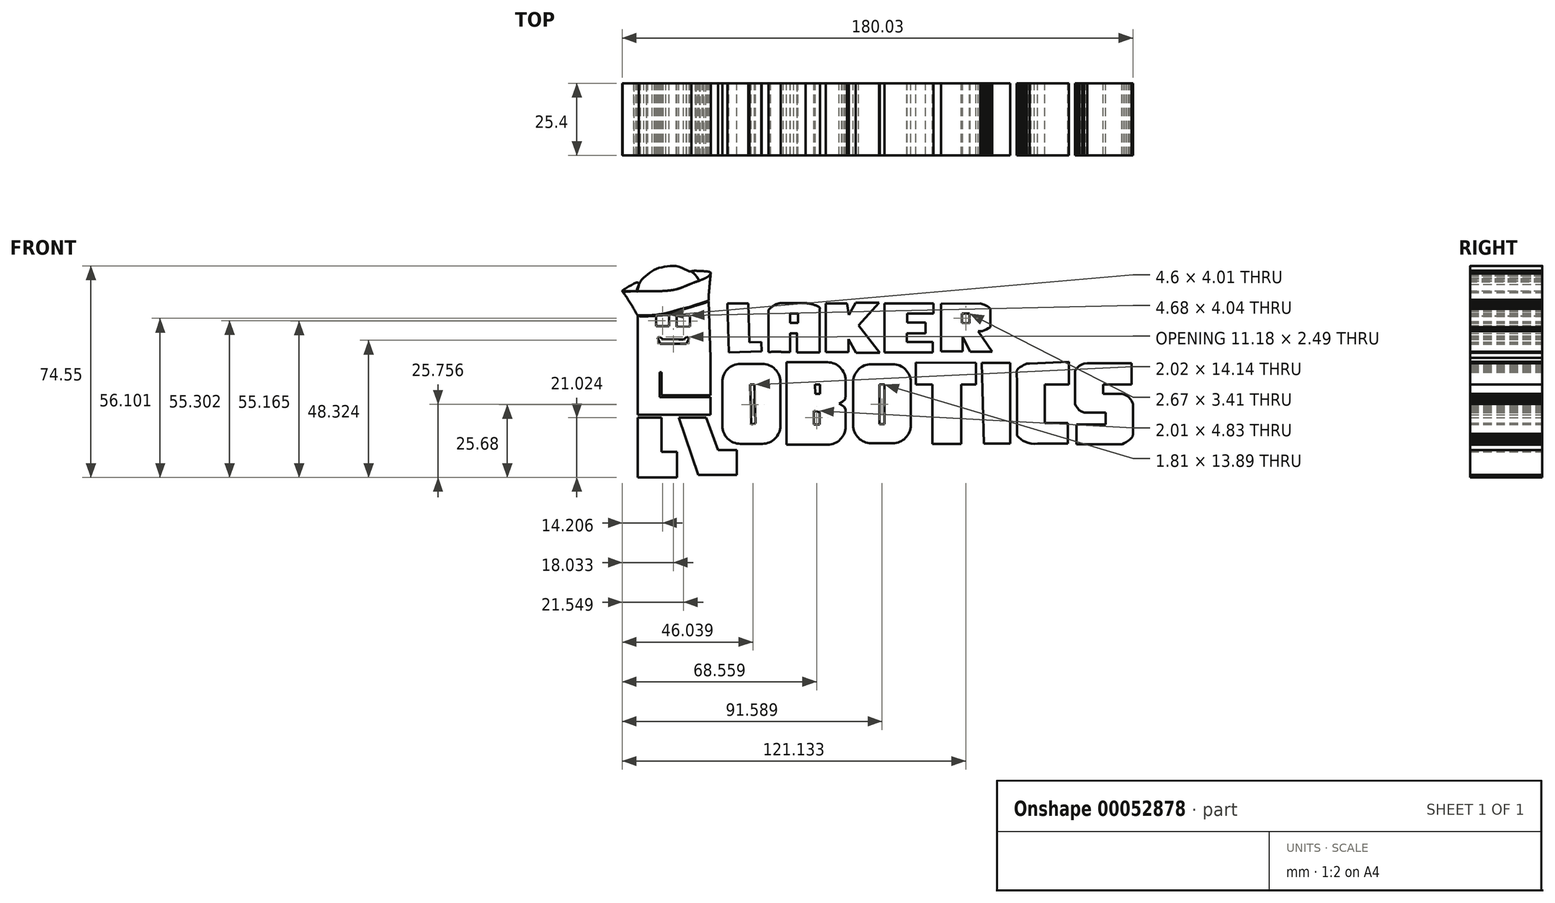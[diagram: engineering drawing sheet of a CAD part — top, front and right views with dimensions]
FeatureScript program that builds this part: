
annotation { "Feature Type Name" : "Feature", "Feature Type Description" : "" }
export const myFeature = defineFeature(function(context is Context, id is Id, definition is map)
    precondition{}
    {
        {
            var Q0;
            Q0=qCreatedBy(makeId("Front.planeOp"),FACE);
            var sketch = newSketch(context, id + "F0", { "sketchPlane" : qUnion([Q0])});
            skLineSegment(sketch, "E0", {"start": v(-88.68, 24.26) * mm, "end": v(-88.68, 9.5) * mm});
            skLineSegment(sketch, "E1", {"start": v(-88.68, -11) * mm, "end": v(-88.68, -32.7) * mm});
            skLineSegment(sketch, "E2", {"start": v(-88.68, -32.7) * mm, "end": v(-74.81, -32.7) * mm});
            skLineSegment(sketch, "E3", {"start": v(-74.81, -32.7) * mm, "end": v(-74.81, -23.66) * mm});
            skLineSegment(sketch, "E4", {"start": v(-74.81, -23.66) * mm, "end": v(-80.24, -23.66) * mm});
            skLineSegment(sketch, "E5", {"start": v(-80.24, -23.66) * mm, "end": v(-80.24, -11.6) * mm});
            skLineSegment(sketch, "E6", {"start": v(-80.24, -11.6) * mm, "end": v(-63.06, -11.6) * mm});
            skLineSegment(sketch, "E7", {"start": v(-63.06, -11.6) * mm, "end": v(-63.06, 9.5) * mm});
            skLineSegment(sketch, "E8", {"start": v(-63.06, 9.5) * mm, "end": v(-88.68, 9.5) * mm});
            skLineSegment(sketch, "E9", {"start": v(-88.68, 0) * mm, "end": v(-88.68, -11) * mm});
            skLineSegment(sketch, "E10", {"start": v(-88.68, 9.5) * mm, "end": v(-88.68, 0) * mm});
            skLineSegment(sketch, "E11", {"start": v(-63.66, 29.38) * mm, "end": v(-63.06, 9.5) * mm});
            skLineSegment(sketch, "E12", {"start": v(-67.28, -31.8) * mm, "end": v(-53.72, -31.8) * mm});
            skLineSegment(sketch, "E13", {"start": v(-53.72, -31.8) * mm, "end": v(-53.72, -23.05) * mm});
            skLineSegment(sketch, "E14", {"start": v(-53.72, -23.05) * mm, "end": v(-60.35, -23.05) * mm});
            skLineSegment(sketch, "E15", {"start": v(-60.35, -23.05) * mm, "end": v(-64.48, -11.6) * mm});
            skLineSegment(sketch, "E16", {"start": v(-64.48, -11.6) * mm, "end": v(-71.65, -11.6) * mm});
            skLineSegment(sketch, "E17", {"start": v(-49.1, 0) * mm, "end": v(-48.68, -14.09) * mm});
            skLineSegment(sketch, "E18", {"start": v(-26.17, 0) * mm, "end": v(-26.08, -3.24) * mm});
            skLineSegment(sketch, "E19", {"start": v(-26.08, -3.24) * mm, "end": v(-24.37, -3.2) * mm});
            skLineSegment(sketch, "E20", {"start": v(-24.37, -3.2) * mm, "end": v(-24.47, 0) * mm});
            skLineSegment(sketch, "E21", {"start": v(-26.17, 0) * mm, "end": v(-24.47, 0) * mm});
            skLineSegment(sketch, "E22", {"start": v(-26.58, -9.26) * mm, "end": v(-26.58, -14.09) * mm});
            skLineSegment(sketch, "E23", {"start": v(-26.58, -14.09) * mm, "end": v(-24.57, -14.09) * mm});
            skLineSegment(sketch, "E24", {"start": v(-24.57, -14.09) * mm, "end": v(-24.57, -9.66) * mm});
            skLineSegment(sketch, "E25", {"start": v(-24.57, -9.66) * mm, "end": v(-26.58, -9.26) * mm});
            skLineSegment(sketch, "E26", {"start": v(-49.1, 0) * mm, "end": v(-47.5, 0.05) * mm});
            skLineSegment(sketch, "E27", {"start": v(-47.5, 0.05) * mm, "end": v(-47.08, -13.69) * mm});
            skLineSegment(sketch, "E28", {"start": v(-48.68, -14.09) * mm, "end": v(-47.08, -13.69) * mm});
            skLineSegment(sketch, "E29", {"start": v(-80.88, 4.41) * mm, "end": v(-80.88, -4.44) * mm});
            skLineSegment(sketch, "E30", {"start": v(-80.88, -4.44) * mm, "end": v(-63.06, -4.44) * mm});
            skLineSegment(sketch, "E31", {"start": v(-63.06, -4.44) * mm, "end": v(-80.88, -4.44) * mm});
            skLineSegment(sketch, "E32", {"start": v(-3.45, 0) * mm, "end": v(-3.45, -13.89) * mm});
            skLineSegment(sketch, "E33", {"start": v(-3.45, -13.89) * mm, "end": v(-1.64, -13.89) * mm});
            skLineSegment(sketch, "E34", {"start": v(-1.64, -13.89) * mm, "end": v(-1.64, 0) * mm});
            skLineSegment(sketch, "E35", {"start": v(-1.64, 0) * mm, "end": v(-3.45, 0) * mm});
            skLineSegment(sketch, "E36", {"start": v(9.43, 7.83) * mm, "end": v(9.43, 0) * mm});
            skLineSegment(sketch, "E37", {"start": v(9.43, 0) * mm, "end": v(15.26, 0) * mm});
            skLineSegment(sketch, "E38", {"start": v(15.26, 0) * mm, "end": v(15.26, -20.93) * mm});
            skLineSegment(sketch, "E39", {"start": v(15.26, -20.93) * mm, "end": v(25.32, -20.93) * mm});
            skLineSegment(sketch, "E40", {"start": v(25.32, -20.93) * mm, "end": v(25.32, 0) * mm});
            skLineSegment(sketch, "E41", {"start": v(25.32, 0) * mm, "end": v(30.54, 0) * mm});
            skLineSegment(sketch, "E42", {"start": v(30.54, 0) * mm, "end": v(30.54, 7.63) * mm});
            skLineSegment(sketch, "E43", {"start": v(30.54, 7.63) * mm, "end": v(9.43, 7.83) * mm});
            skLineSegment(sketch, "E44", {"start": v(32.56, 7.63) * mm, "end": v(42.61, 7.63) * mm});
            skLineSegment(sketch, "E45", {"start": v(42.61, 7.63) * mm, "end": v(42.61, -20.73) * mm});
            skLineSegment(sketch, "E46", {"start": v(42.61, -20.73) * mm, "end": v(33.36, -20.73) * mm});
            skLineSegment(sketch, "E47", {"start": v(33.36, -20.73) * mm, "end": v(32.56, 7.63) * mm});
            skLineSegment(sketch, "E48", {"start": v(63.33, 8.04) * mm, "end": v(63.33, 0) * mm});
            skLineSegment(sketch, "E49", {"start": v(63.33, 0) * mm, "end": v(54.88, 0) * mm});
            skLineSegment(sketch, "E50", {"start": v(54.88, 0) * mm, "end": v(54.88, -13.49) * mm});
            skLineSegment(sketch, "E51", {"start": v(54.88, -13.49) * mm, "end": v(62.93, -13.49) * mm});
            skLineSegment(sketch, "E52", {"start": v(62.93, -13.49) * mm, "end": v(62.93, -20.73) * mm});
            skLineSegment(sketch, "E53", {"start": v(62.93, -20.73) * mm, "end": v(52.27, -20.73) * mm});
            skLineSegment(sketch, "E54", {"start": v(52.27, -20.73) * mm, "end": v(62.93, -20.73) * mm});
            skLineSegment(sketch, "E55", {"start": v(45.03, -16.9) * mm, "end": v(45.03, 0) * mm});
            skLineSegment(sketch, "E56", {"start": v(49.45, 7.43) * mm, "end": v(63.33, 8.04) * mm});
            skLineSegment(sketch, "E57", {"start": v(-12.7, 0.88) * mm, "end": v(-12.7, -14.3) * mm});
            skPoint(sketch, "E57.endSnap0", {"position": v(62.93, -17.1) * mm});
            skLineSegment(sketch, "E58", {"start": v(-6.35, -20.64) * mm, "end": v(1.23, -20.64) * mm});
            skLineSegment(sketch, "E59", {"start": v(-6.35, 7.23) * mm, "end": v(1.23, 7.23) * mm});
            skLineSegment(sketch, "E60", {"start": v(7.58, 0.88) * mm, "end": v(7.58, -14.3) * mm});
            skLineSegment(sketch, "E61", {"start": v(-36.19, 7.89) * mm, "end": v(-36.19, -21.16) * mm});
            skLineSegment(sketch, "E62", {"start": v(-36.19, -21.16) * mm, "end": v(-21.75, -21.16) * mm});
            skLineSegment(sketch, "E63", {"start": v(-36.19, 7.89) * mm, "end": v(-21.75, 7.89) * mm});
            skLineSegment(sketch, "E64", {"start": v(-15.4, 1.54) * mm, "end": v(-15.4, -3.7) * mm});
            skLineSegment(sketch, "E65", {"start": v(-15.4, -8.63) * mm, "end": v(-15.4, -14.8) * mm});
            skLineSegment(sketch, "E66", {"start": v(-58.86, 0.96) * mm, "end": v(-58.86, -14.5) * mm});
            skLineSegment(sketch, "E67", {"start": v(-52.32, -20.85) * mm, "end": v(-44.73, -20.85) * mm});
            skLineSegment(sketch, "E68", {"start": v(-38.38, 0.96) * mm, "end": v(-38.38, -14.5) * mm});
            skLineSegment(sketch, "E69", {"start": v(-52.51, 7.3) * mm, "end": v(-44.73, 7.3) * mm});
            skLineSegment(sketch, "E70", {"start": v(-82.23, 24.26) * mm, "end": v(-82.23, 20.6) * mm});
            skLineSegment(sketch, "E71", {"start": v(-82.23, 20.6) * mm, "end": v(-77.62, 20.6) * mm});
            skLineSegment(sketch, "E72", {"start": v(-77.62, 20.6) * mm, "end": v(-77.62, 24.6) * mm});
            skLineSegment(sketch, "E73", {"start": v(-77.62, 24.6) * mm, "end": v(-82.23, 24.26) * mm});
            skLineSegment(sketch, "E74", {"start": v(-74.92, 24.36) * mm, "end": v(-74.92, 20.44) * mm});
            skLineSegment(sketch, "E75", {"start": v(-74.92, 20.44) * mm, "end": v(-70.24, 20.45) * mm});
            skLineSegment(sketch, "E76", {"start": v(-70.24, 20.45) * mm, "end": v(-70.24, 24.49) * mm});
            skLineSegment(sketch, "E77", {"start": v(-70.24, 24.49) * mm, "end": v(-74.92, 24.36) * mm});
            skLineSegment(sketch, "E78", {"start": v(-81.69, 16.53) * mm, "end": v(-80.8, 14.38) * mm});
            skLineSegment(sketch, "E79", {"start": v(-80.8, 14.38) * mm, "end": v(-71.52, 14.38) * mm});
            skLineSegment(sketch, "E80", {"start": v(-71.52, 14.38) * mm, "end": v(-70.5, 16.41) * mm});
            skLineSegment(sketch, "E81", {"start": v(-70.5, 16.41) * mm, "end": v(-71.42, 16.87) * mm});
            skLineSegment(sketch, "E82", {"start": v(-71.42, 16.87) * mm, "end": v(-72.48, 16) * mm});
            skLineSegment(sketch, "E83", {"start": v(-72.48, 16) * mm, "end": v(-79.65, 16) * mm});
            skLineSegment(sketch, "E84", {"start": v(-79.65, 16) * mm, "end": v(-80.97, 16.77) * mm});
            skLineSegment(sketch, "E85", {"start": v(-80.97, 16.77) * mm, "end": v(-81.69, 16.53) * mm});
            skLineSegment(sketch, "E86", {"start": v(-62.91, 39.4) * mm, "end": v(-63.66, 29.38) * mm});
            skLineSegment(sketch, "E87", {"start": v(-94.06, 32.86) * mm, "end": v(-88.68, 24.26) * mm});
            skLineSegment(sketch, "E88", {"start": v(-57.08, 28.59) * mm, "end": v(-56.56, 11.4) * mm});
            skLineSegment(sketch, "E89", {"start": v(-56.56, 11.4) * mm, "end": v(-45, 11.74) * mm});
            skLineSegment(sketch, "E90", {"start": v(-45, 11.74) * mm, "end": v(-45.1, 15.07) * mm});
            skLineSegment(sketch, "E91", {"start": v(-45.1, 15.07) * mm, "end": v(-49.3, 14.94) * mm});
            skLineSegment(sketch, "E92", {"start": v(-49.3, 14.94) * mm, "end": v(-49.71, 28.7) * mm});
            skLineSegment(sketch, "E93", {"start": v(-49.71, 28.7) * mm, "end": v(-57.08, 28.59) * mm});
            skLineSegment(sketch, "E94", {"start": v(-42.57, 26.31) * mm, "end": v(-42.57, 11.52) * mm});
            skLineSegment(sketch, "E95", {"start": v(-42.57, 11.52) * mm, "end": v(-34.9, 11.52) * mm});
            skLineSegment(sketch, "E96", {"start": v(-34.9, 11.52) * mm, "end": v(-34.9, 18.06) * mm});
            skLineSegment(sketch, "E97", {"start": v(-34.9, 18.06) * mm, "end": v(-32.48, 18.06) * mm});
            skLineSegment(sketch, "E98", {"start": v(-32.48, 18.06) * mm, "end": v(-32.48, 11.38) * mm});
            skLineSegment(sketch, "E99", {"start": v(-32.48, 11.38) * mm, "end": v(-24.51, 11.38) * mm});
            skLineSegment(sketch, "E100", {"start": v(-24.51, 11.38) * mm, "end": v(-24.51, 26.6) * mm});
            skLineSegment(sketch, "E101", {"start": v(-38.3, 28.73) * mm, "end": v(-29.5, 28.73) * mm});
            skLineSegment(sketch, "E102", {"start": v(-34.9, 25.03) * mm, "end": v(-34.9, 21.76) * mm});
            skLineSegment(sketch, "E103", {"start": v(-34.9, 21.76) * mm, "end": v(-32.2, 21.76) * mm});
            skLineSegment(sketch, "E104", {"start": v(-32.2, 21.76) * mm, "end": v(-32.2, 25.03) * mm});
            skLineSegment(sketch, "E105", {"start": v(-32.2, 25.03) * mm, "end": v(-34.9, 25.03) * mm});
            skLineSegment(sketch, "E106", {"start": v(-14.84, 28.59) * mm, "end": v(-22.38, 28.59) * mm});
            skLineSegment(sketch, "E107", {"start": v(-22.38, 28.59) * mm, "end": v(-22.38, 11.52) * mm});
            skLineSegment(sketch, "E108", {"start": v(-22.38, 11.52) * mm, "end": v(-14.41, 11.52) * mm});
            skLineSegment(sketch, "E109", {"start": v(-14.41, 11.52) * mm, "end": v(-14.41, 16.07) * mm});
            skLineSegment(sketch, "E110", {"start": v(-14.41, 16.07) * mm, "end": v(-11.71, 11.24) * mm});
            skLineSegment(sketch, "E111", {"start": v(-11.71, 11.24) * mm, "end": v(-3.32, 11.24) * mm});
            skLineSegment(sketch, "E112", {"start": v(-3.32, 11.24) * mm, "end": v(-10.86, 20.9) * mm});
            skLineSegment(sketch, "E113", {"start": v(-10.86, 20.9) * mm, "end": v(-3.6, 28.87) * mm});
            skLineSegment(sketch, "E114", {"start": v(-3.6, 28.87) * mm, "end": v(-11.85, 28.87) * mm});
            skLineSegment(sketch, "E115", {"start": v(-11.85, 28.87) * mm, "end": v(-14.27, 24.6) * mm});
            skLineSegment(sketch, "E116", {"start": v(-14.27, 24.6) * mm, "end": v(-14.84, 28.59) * mm});
            skLineSegment(sketch, "E117", {"start": v(-1.61, 28.59) * mm, "end": v(-1.61, 11.38) * mm});
            skLineSegment(sketch, "E118", {"start": v(-1.61, 11.38) * mm, "end": v(15.3, 11.38) * mm});
            skLineSegment(sketch, "E119", {"start": v(15.3, 11.38) * mm, "end": v(15.3, 15.08) * mm});
            skLineSegment(sketch, "E120", {"start": v(15.3, 15.08) * mm, "end": v(6.2, 15.08) * mm});
            skLineSegment(sketch, "E121", {"start": v(6.2, 15.08) * mm, "end": v(6.2, 18.06) * mm});
            skLineSegment(sketch, "E122", {"start": v(6.2, 18.06) * mm, "end": v(12.75, 18.06) * mm});
            skLineSegment(sketch, "E123", {"start": v(12.75, 18.06) * mm, "end": v(12.75, 21.9) * mm});
            skLineSegment(sketch, "E124", {"start": v(12.75, 21.9) * mm, "end": v(6.35, 21.9) * mm});
            skLineSegment(sketch, "E125", {"start": v(6.35, 21.9) * mm, "end": v(6.35, 25.03) * mm});
            skLineSegment(sketch, "E126", {"start": v(6.35, 25.03) * mm, "end": v(15.6, 25.03) * mm});
            skLineSegment(sketch, "E127", {"start": v(15.6, 25.03) * mm, "end": v(15.6, 28.59) * mm});
            skLineSegment(sketch, "E128", {"start": v(15.6, 28.59) * mm, "end": v(-1.61, 28.59) * mm});
            skPoint(sketch, "E129.6.internal.snap0", {"position": v(-63.29, 34.39) * mm});
            skFitSpline(sketch, "E129", {"points": [v(-88.68, 24.26) * mm, v(-82.83, 24.26) * mm, v(-75.78, 25.68) * mm, v(-63.66, 29.38) * mm, v(-63.62, 29.96) * mm, v(-62.91, 39.4) * mm, v(-63.29, 38.66) * mm, v(-70.15, 35.5) * mm, v(-77.62, 33.2) * mm, v(-94.06, 32.86) * mm, v(-93.78, 32.4) * mm, v(-89.18, 25.06) * mm, v(-88.68, 24.26) * mm]});
            skFitSpline(sketch, "E130", {"points": [v(-94.06, 32.86) * mm, v(-91.65, 34.7) * mm, v(-88.37, 35.84) * mm, v(-88.94, 32.95) * mm, v(-89.32, 32.95) * mm, v(-94.06, 32.86) * mm]});
            skFitSpline(sketch, "E131", {"points": [v(-69.7, 39.96) * mm, v(-66.1, 40.04) * mm, v(-62.91, 39.4) * mm, v(-64.66, 37.64) * mm, v(-66.76, 36.73) * mm, v(-67, 36.64) * mm, v(-68.34, 38.66) * mm, v(-69.7, 39.96) * mm]});
            skFitSpline(sketch, "E132", {"points": [v(-88.94, 32.95) * mm, v(-87.97, 35.93) * mm, v(-85.54, 38.6) * mm, v(-82.35, 40.76) * mm, v(-78.48, 41.64) * mm, v(-74, 41.56) * mm, v(-70.41, 39.96) * mm, v(-69.7, 39.96) * mm, v(-68.34, 38.66) * mm, v(-67, 36.64) * mm, v(-67.47, 36.47) * mm, v(-71.33, 35) * mm, v(-75.64, 33.5) * mm, v(-80.95, 32.98) * mm, v(-85.62, 32.92) * mm, v(-88.45, 32.94) * mm, v(-88.94, 32.95) * mm]});
            skFitSpline(sketch, "E133", {"points": [v(-38.3, 28.73) * mm, v(-40.5, 28.02) * mm, v(-42.57, 26.31) * mm, v(-42.57, 24.89) * mm, v(-42.57, 11.52) * mm, v(-41.76, 11.52) * mm, v(-34.9, 11.52) * mm, v(-34.9, 11.73) * mm, v(-34.9, 14.3) * mm, v(-34.9, 18.06) * mm, v(-34.84, 18.06) * mm, v(-33.69, 18.06) * mm, v(-32.48, 18.06) * mm, v(-32.48, 18.04) * mm, v(-32.48, 17.21) * mm, v(-32.48, 16.46) * mm, v(-32.48, 15.64) * mm, v(-32.48, 14.72) * mm, v(-32.48, 13.62) * mm, v(-32.48, 11.85) * mm, v(-32.48, 11.38) * mm, v(-32.35, 11.38) * mm, v(-24.51, 11.38) * mm, v(-24.51, 11.4) * mm, v(-24.51, 11.66) * mm, v(-24.51, 12.58) * mm, v(-24.51, 16.6) * mm, v(-24.51, 22.3) * mm, v(-24.51, 26.6) * mm, v(-24.51, 27.11) * mm, v(-26.4, 28.13) * mm, v(-29.5, 28.73) * mm, v(-34.44, 28.73) * mm, v(-38.3, 28.73) * mm]});
            skLineSegment(sketch, "E134", {"start": v(49.45, 7.43) * mm, "end": v(48.5, 7.43) * mm});
            skLineSegment(sketch, "E135", {"start": v(48.5, 7.43) * mm, "end": v(48, 7.19) * mm});
            skLineSegment(sketch, "E136", {"start": v(48, 7.19) * mm, "end": v(47.36, 6.93) * mm});
            skLineSegment(sketch, "E137", {"start": v(47.36, 6.93) * mm, "end": v(46.82, 6.57) * mm});
            skLineSegment(sketch, "E138", {"start": v(46.82, 6.57) * mm, "end": v(46.13, 6.13) * mm});
            skLineSegment(sketch, "E139", {"start": v(46.13, 6.13) * mm, "end": v(45.5, 5.63) * mm});
            skLineSegment(sketch, "E140", {"start": v(45.5, 5.63) * mm, "end": v(44.92, 4.85) * mm});
            skLineSegment(sketch, "E141", {"start": v(44.92, 4.85) * mm, "end": v(45.03, 0) * mm});
            skLineSegment(sketch, "E142", {"start": v(45.03, -16.9) * mm, "end": v(45.03, -17.94) * mm});
            skLineSegment(sketch, "E143", {"start": v(45.03, -17.94) * mm, "end": v(45.6, -18.5) * mm});
            skLineSegment(sketch, "E144", {"start": v(45.6, -18.5) * mm, "end": v(46.41, -19.21) * mm});
            skLineSegment(sketch, "E145", {"start": v(46.41, -19.21) * mm, "end": v(47.15, -19.78) * mm});
            skLineSegment(sketch, "E146", {"start": v(47.15, -19.78) * mm, "end": v(47.96, -20.08) * mm});
            skLineSegment(sketch, "E147", {"start": v(47.96, -20.08) * mm, "end": v(48.97, -20.51) * mm});
            skLineSegment(sketch, "E148", {"start": v(48.97, -20.51) * mm, "end": v(50.05, -20.75) * mm});
            skLineSegment(sketch, "E149", {"start": v(50.05, -20.75) * mm, "end": v(51.13, -20.85) * mm});
            skLineSegment(sketch, "E150", {"start": v(51.13, -20.85) * mm, "end": v(52.27, -20.73) * mm});
            skArc(sketch, "E151.filletArc", {"start": v(-6.35, 7.23) * mm, "mid": v(-10.84, 5.37) * mm, "end": v(-12.7, 0.88) * mm});
            skArc(sketch, "E152.filletArc", {"start": v(7.58, 0.88) * mm, "mid": v(5.72, 5.37) * mm, "end": v(1.23, 7.23) * mm});
            skPoint(sketch, "E153.newPointA", {"position": v(-12.7, -17.1) * mm});
            skArc(sketch, "E153.filletArc", {"start": v(-12.7, -14.3) * mm, "mid": v(-10.84, -18.78) * mm, "end": v(-6.35, -20.64) * mm});
            skArc(sketch, "E154.filletArc", {"start": v(1.23, -20.64) * mm, "mid": v(5.72, -18.78) * mm, "end": v(7.58, -14.3) * mm});
            skArc(sketch, "E155.filletArc", {"start": v(-15.4, 1.54) * mm, "mid": v(-17.26, 6.03) * mm, "end": v(-21.75, 7.89) * mm});
            skArc(sketch, "E156.filletArc", {"start": v(-21.75, -21.16) * mm, "mid": v(-17.26, -19.3) * mm, "end": v(-15.4, -14.8) * mm});
            skLineSegment(sketch, "E157", {"start": v(-17.69, -6.73) * mm, "end": v(-16.54, -6.08) * mm});
            skLineSegment(sketch, "E158", {"start": v(-16.54, -6.08) * mm, "end": v(-15.58, -5.19) * mm});
            skLineSegment(sketch, "E159", {"start": v(-15.58, -5.19) * mm, "end": v(-15.4, -3.7) * mm});
            skLineSegment(sketch, "E160", {"start": v(-17.69, -6.73) * mm, "end": v(-16.75, -7.13) * mm});
            skLineSegment(sketch, "E161", {"start": v(-16.75, -7.13) * mm, "end": v(-15.95, -7.79) * mm});
            skLineSegment(sketch, "E162", {"start": v(-15.95, -7.79) * mm, "end": v(-15.39, -8.7) * mm});
            skLineSegment(sketch, "E163", {"start": v(-15.39, -8.7) * mm, "end": v(-15.4, -8.63) * mm});
            skArc(sketch, "E164.filletArc", {"start": v(-52.51, 7.3) * mm, "mid": v(-57, 5.45) * mm, "end": v(-58.86, 0.96) * mm});
            skArc(sketch, "E165.filletArc", {"start": v(-38.38, 0.96) * mm, "mid": v(-40.24, 5.45) * mm, "end": v(-44.73, 7.3) * mm});
            skArc(sketch, "E166.filletArc", {"start": v(-44.73, -20.85) * mm, "mid": v(-40.24, -19) * mm, "end": v(-38.38, -14.5) * mm});
            skLineSegment(sketch, "E167", {"start": v(-52.32, -20.85) * mm, "end": v(-52.51, -20.85) * mm});
            skArc(sketch, "E168.filletArc", {"start": v(-58.86, -14.5) * mm, "mid": v(-57, -19) * mm, "end": v(-52.51, -20.85) * mm});
            skLineSegment(sketch, "E169", {"start": v(-74.25, -11.6) * mm, "end": v(-67.28, -31.8) * mm});
            skLineSegment(sketch, "E170", {"start": v(-80.24, -11.6) * mm, "end": v(-88.68, -11.6) * mm});
            skLineSegment(sketch, "E171", {"start": v(-80.88, 4.41) * mm, "end": v(-80.3, 4.41) * mm});
            skLineSegment(sketch, "E172", {"start": v(-80.3, 4.41) * mm, "end": v(-80.3, -3.8) * mm});
            skLineSegment(sketch, "E173", {"start": v(-80.3, -3.8) * mm, "end": v(-63.06, -3.8) * mm});
            skLineSegment(sketch, "E174", {"start": v(-63.06, -3.8) * mm, "end": v(-63.06, -4.44) * mm});
            skLineSegment(sketch, "E175", {"start": v(-63.06, -10.58) * mm, "end": v(-88.68, -10.58) * mm});
            skLineSegment(sketch, "E176", {"start": v(-88.68, 10.11) * mm, "end": v(-63.08, 10.11) * mm});
            skLineSegment(sketch, "E177", {"start": v(-88.68, 10.11) * mm, "end": v(-88.68, 9.5) * mm});
            skLineSegment(sketch, "E178", {"start": v(-63.08, 10.11) * mm, "end": v(-63.06, 9.5) * mm});
            skLineSegment(sketch, "E179", {"start": v(-88.86, 24.55) * mm, "end": v(-87.68, 24.41) * mm});
            skLineSegment(sketch, "E180", {"start": v(-87.68, 24.41) * mm, "end": v(-86.54, 24.42) * mm});
            skLineSegment(sketch, "E181", {"start": v(-86.54, 24.42) * mm, "end": v(-85.24, 24.47) * mm});
            skLineSegment(sketch, "E182", {"start": v(-85.24, 24.47) * mm, "end": v(-83.56, 24.53) * mm});
            skLineSegment(sketch, "E183", {"start": v(-83.56, 24.53) * mm, "end": v(-82.4, 24.62) * mm});
            skLineSegment(sketch, "E184", {"start": v(-82.4, 24.62) * mm, "end": v(-81.11, 24.83) * mm});
            skLineSegment(sketch, "E185", {"start": v(-81.11, 24.83) * mm, "end": v(-80.18, 24.98) * mm});
            skLineSegment(sketch, "E186", {"start": v(-80.18, 24.98) * mm, "end": v(-78.82, 25.25) * mm});
            skLineSegment(sketch, "E187", {"start": v(-78.82, 25.25) * mm, "end": v(-77.24, 25.65) * mm});
            skLineSegment(sketch, "E188", {"start": v(-77.24, 25.65) * mm, "end": v(-75.2, 26.19) * mm});
            skLineSegment(sketch, "E189", {"start": v(-75.2, 26.19) * mm, "end": v(-73.38, 26.67) * mm});
            skLineSegment(sketch, "E190", {"start": v(-73.38, 26.67) * mm, "end": v(-70.5, 27.43) * mm});
            skLineSegment(sketch, "E191", {"start": v(-70.5, 27.43) * mm, "end": v(-68.35, 28.1) * mm});
            skLineSegment(sketch, "E192", {"start": v(-68.35, 28.1) * mm, "end": v(-65.9, 28.87) * mm});
            skLineSegment(sketch, "E193", {"start": v(-65.9, 28.87) * mm, "end": v(-63.58, 29.7) * mm});
            skLineSegment(sketch, "E194", {"start": v(-63.58, 29.7) * mm, "end": v(-63.56, 29.51) * mm});
            skLineSegment(sketch, "E195", {"start": v(-63.56, 29.51) * mm, "end": v(-63.58, 29.46) * mm});
            skLineSegment(sketch, "E196", {"start": v(-63.58, 29.46) * mm, "end": v(-63.64, 29.38) * mm});
            skLineSegment(sketch, "E197", {"start": v(-63.64, 29.38) * mm, "end": v(-64.17, 29.1) * mm});
            skLineSegment(sketch, "E198", {"start": v(-64.17, 29.1) * mm, "end": v(-64.76, 28.92) * mm});
            skLineSegment(sketch, "E199", {"start": v(-64.76, 28.92) * mm, "end": v(-65.57, 28.63) * mm});
            skLineSegment(sketch, "E200", {"start": v(-65.57, 28.63) * mm, "end": v(-67.18, 28.12) * mm});
            skLineSegment(sketch, "E201", {"start": v(-67.18, 28.12) * mm, "end": v(-68.65, 27.7) * mm});
            skLineSegment(sketch, "E202", {"start": v(-68.65, 27.7) * mm, "end": v(-70.9, 27.04) * mm});
            skLineSegment(sketch, "E203", {"start": v(-70.9, 27.04) * mm, "end": v(-72.9, 26.47) * mm});
            skLineSegment(sketch, "E204", {"start": v(-72.9, 26.47) * mm, "end": v(-74.1, 26.14) * mm});
            skLineSegment(sketch, "E205", {"start": v(-74.1, 26.14) * mm, "end": v(-75.04, 25.88) * mm});
            skLineSegment(sketch, "E206", {"start": v(-75.04, 25.88) * mm, "end": v(-75.78, 25.68) * mm});
            skLineSegment(sketch, "E207", {"start": v(-75.78, 25.68) * mm, "end": v(-76.6, 25.46) * mm});
            skLineSegment(sketch, "E208", {"start": v(-76.6, 25.46) * mm, "end": v(-77.32, 25.27) * mm});
            skLineSegment(sketch, "E209", {"start": v(-77.32, 25.27) * mm, "end": v(-78.28, 25.03) * mm});
            skLineSegment(sketch, "E210", {"start": v(-78.28, 25.03) * mm, "end": v(-79.17, 24.83) * mm});
            skLineSegment(sketch, "E211", {"start": v(-79.17, 24.83) * mm, "end": v(-79.7, 24.7) * mm});
            skLineSegment(sketch, "E212", {"start": v(-79.7, 24.7) * mm, "end": v(-80.33, 24.6) * mm});
            skLineSegment(sketch, "E213", {"start": v(-80.33, 24.6) * mm, "end": v(-80.9, 24.5) * mm});
            skLineSegment(sketch, "E214", {"start": v(-80.9, 24.5) * mm, "end": v(-81.34, 24.42) * mm});
            skLineSegment(sketch, "E215", {"start": v(-81.34, 24.42) * mm, "end": v(-82.06, 24.33) * mm});
            skLineSegment(sketch, "E216", {"start": v(-82.06, 24.33) * mm, "end": v(-82.88, 24.25) * mm});
            skLineSegment(sketch, "E217", {"start": v(-82.88, 24.25) * mm, "end": v(-83.6, 24.2) * mm});
            skLineSegment(sketch, "E218", {"start": v(-83.6, 24.2) * mm, "end": v(-85.15, 24.1) * mm});
            skLineSegment(sketch, "E219", {"start": v(-85.15, 24.1) * mm, "end": v(-86.6, 24.08) * mm});
            skLineSegment(sketch, "E220", {"start": v(-86.6, 24.08) * mm, "end": v(-87.42, 24.1) * mm});
            skLineSegment(sketch, "E221", {"start": v(-87.42, 24.1) * mm, "end": v(-88.06, 24.14) * mm});
            skLineSegment(sketch, "E222", {"start": v(-88.06, 24.14) * mm, "end": v(-88.56, 24.22) * mm});
            skLineSegment(sketch, "E223", {"start": v(-88.56, 24.22) * mm, "end": v(-88.67, 24.26) * mm});
            skLineSegment(sketch, "E224", {"start": v(-88.67, 24.26) * mm, "end": v(-88.86, 24.55) * mm});
            skLineSegment(sketch, "E225", {"start": v(18.23, 28.57) * mm, "end": v(18.23, 11.78) * mm});
            skLineSegment(sketch, "E226", {"start": v(18.23, 11.78) * mm, "end": v(25.84, 11.78) * mm});
            skLineSegment(sketch, "E227", {"start": v(25.84, 11.78) * mm, "end": v(25.84, 16.79) * mm});
            skLineSegment(sketch, "E228", {"start": v(25.84, 16.79) * mm, "end": v(28.56, 11.6) * mm});
            skLineSegment(sketch, "E229", {"start": v(28.56, 11.6) * mm, "end": v(36.35, 11.6) * mm});
            skLineSegment(sketch, "E230", {"start": v(36.35, 11.6) * mm, "end": v(31.35, 18.88) * mm});
            skLineSegment(sketch, "E231", {"start": v(31.35, 18.88) * mm, "end": v(32.69, 18.88) * mm});
            skLineSegment(sketch, "E232", {"start": v(32.69, 18.88) * mm, "end": v(33.4, 19.1) * mm});
            skLineSegment(sketch, "E233", {"start": v(33.4, 19.1) * mm, "end": v(34.28, 19.46) * mm});
            skLineSegment(sketch, "E234", {"start": v(34.28, 19.46) * mm, "end": v(34.96, 19.86) * mm});
            skLineSegment(sketch, "E235", {"start": v(34.96, 19.86) * mm, "end": v(35.66, 20.28) * mm});
            skLineSegment(sketch, "E236", {"start": v(35.66, 20.28) * mm, "end": v(35.66, 22.13) * mm});
            skLineSegment(sketch, "E237", {"start": v(35.66, 22.13) * mm, "end": v(35.66, 26.77) * mm});
            skLineSegment(sketch, "E238", {"start": v(35.66, 26.77) * mm, "end": v(35.35, 27.02) * mm});
            skLineSegment(sketch, "E239", {"start": v(35.35, 27.02) * mm, "end": v(35, 27.4) * mm});
            skLineSegment(sketch, "E240", {"start": v(35, 27.4) * mm, "end": v(34.62, 27.65) * mm});
            skLineSegment(sketch, "E241", {"start": v(34.62, 27.65) * mm, "end": v(34.12, 27.9) * mm});
            skLineSegment(sketch, "E242", {"start": v(34.12, 27.9) * mm, "end": v(33.58, 28.16) * mm});
            skLineSegment(sketch, "E243", {"start": v(33.58, 28.16) * mm, "end": v(32.85, 28.35) * mm});
            skLineSegment(sketch, "E244", {"start": v(32.85, 28.35) * mm, "end": v(32.09, 28.6) * mm});
            skLineSegment(sketch, "E245", {"start": v(32.09, 28.6) * mm, "end": v(18.23, 28.57) * mm});
            skLineSegment(sketch, "E246", {"start": v(25.67, 25.1) * mm, "end": v(25.67, 21.77) * mm});
            skLineSegment(sketch, "E247", {"start": v(25.67, 21.77) * mm, "end": v(28.34, 21.7) * mm});
            skLineSegment(sketch, "E248", {"start": v(28.34, 21.7) * mm, "end": v(28.34, 25.07) * mm});
            skLineSegment(sketch, "E249", {"start": v(28.34, 25.07) * mm, "end": v(25.67, 25.1) * mm});
            skLineSegment(sketch, "E250", {"start": v(65.48, 4.73) * mm, "end": v(65.48, -6.75) * mm});
            skLineSegment(sketch, "E251", {"start": v(69.97, -9.9) * mm, "end": v(76.35, -9.9) * mm});
            skLineSegment(sketch, "E252", {"start": v(76.35, -9.9) * mm, "end": v(76.35, -14) * mm});
            skLineSegment(sketch, "E253", {"start": v(76.35, -14) * mm, "end": v(66.01, -14) * mm});
            skLineSegment(sketch, "E254", {"start": v(66.01, -14) * mm, "end": v(66.01, -20.98) * mm});
            skLineSegment(sketch, "E255", {"start": v(66.01, -20.98) * mm, "end": v(81.18, -20.98) * mm});
            skLineSegment(sketch, "E256", {"start": v(69.86, 7.51) * mm, "end": v(85.4, 7.51) * mm});
            skLineSegment(sketch, "E257", {"start": v(85.4, 7.51) * mm, "end": v(85.4, 0) * mm});
            skLineSegment(sketch, "E258", {"start": v(85.4, 0) * mm, "end": v(75.42, 0) * mm});
            skLineSegment(sketch, "E259", {"start": v(75.42, 0) * mm, "end": v(75.42, -3.25) * mm});
            skLineSegment(sketch, "E260", {"start": v(75.42, -3.25) * mm, "end": v(81.1, -3.25) * mm});
            skLineSegment(sketch, "E261", {"start": v(85.9, -6.78) * mm, "end": v(85.9, -17.3) * mm});
            skLineSegment(sketch, "E262", {"start": v(65.48, -6.75) * mm, "end": v(65.82, -7.38) * mm});
            skLineSegment(sketch, "E263", {"start": v(65.82, -7.38) * mm, "end": v(66.38, -8.16) * mm});
            skLineSegment(sketch, "E264", {"start": v(66.38, -8.16) * mm, "end": v(66.96, -8.92) * mm});
            skLineSegment(sketch, "E265", {"start": v(66.96, -8.92) * mm, "end": v(67.8, -9.46) * mm});
            skLineSegment(sketch, "E266", {"start": v(67.8, -9.46) * mm, "end": v(68.87, -9.82) * mm});
            skLineSegment(sketch, "E267", {"start": v(68.87, -9.82) * mm, "end": v(69.34, -9.9) * mm});
            skLineSegment(sketch, "E268", {"start": v(69.34, -9.9) * mm, "end": v(69.97, -9.9) * mm});
            skLineSegment(sketch, "E269", {"start": v(65.48, 4.73) * mm, "end": v(65.8, 5.4) * mm});
            skLineSegment(sketch, "E270", {"start": v(65.8, 5.4) * mm, "end": v(66.26, 5.96) * mm});
            skLineSegment(sketch, "E271", {"start": v(66.26, 5.96) * mm, "end": v(67.07, 6.67) * mm});
            skLineSegment(sketch, "E272", {"start": v(67.07, 6.67) * mm, "end": v(68, 7.19) * mm});
            skLineSegment(sketch, "E273", {"start": v(68, 7.19) * mm, "end": v(68.75, 7.49) * mm});
            skLineSegment(sketch, "E274", {"start": v(68.75, 7.49) * mm, "end": v(69.86, 7.51) * mm});
            skLineSegment(sketch, "E275", {"start": v(81.1, -3.25) * mm, "end": v(82.04, -3.25) * mm});
            skLineSegment(sketch, "E276", {"start": v(82.04, -3.25) * mm, "end": v(82.92, -3.48) * mm});
            skLineSegment(sketch, "E277", {"start": v(82.92, -3.48) * mm, "end": v(83.68, -3.85) * mm});
            skLineSegment(sketch, "E278", {"start": v(83.68, -3.85) * mm, "end": v(84.38, -4.43) * mm});
            skLineSegment(sketch, "E279", {"start": v(84.38, -4.43) * mm, "end": v(85.1, -5.15) * mm});
            skLineSegment(sketch, "E280", {"start": v(85.1, -5.15) * mm, "end": v(85.49, -5.68) * mm});
            skLineSegment(sketch, "E281", {"start": v(85.49, -5.68) * mm, "end": v(85.82, -6.52) * mm});
            skLineSegment(sketch, "E282", {"start": v(85.82, -6.52) * mm, "end": v(85.9, -6.78) * mm});
            skLineSegment(sketch, "E283", {"start": v(81.18, -20.98) * mm, "end": v(82.12, -20.98) * mm});
            skLineSegment(sketch, "E284", {"start": v(82.12, -20.98) * mm, "end": v(82.83, -20.65) * mm});
            skLineSegment(sketch, "E285", {"start": v(82.83, -20.65) * mm, "end": v(83.57, -20.22) * mm});
            skLineSegment(sketch, "E286", {"start": v(83.57, -20.22) * mm, "end": v(84.29, -19.74) * mm});
            skLineSegment(sketch, "E287", {"start": v(84.29, -19.74) * mm, "end": v(84.9, -19.22) * mm});
            skLineSegment(sketch, "E288", {"start": v(84.9, -19.22) * mm, "end": v(85.47, -18.7) * mm});
            skLineSegment(sketch, "E289", {"start": v(85.47, -18.7) * mm, "end": v(85.88, -18.23) * mm});
            skLineSegment(sketch, "E290", {"start": v(85.88, -18.23) * mm, "end": v(85.9, -17.3) * mm});
            skSolve(sketch);
        }
        {
            var Q0;
            {var subQ1=sQuery(id+"F0.wireOp",EDGE,"E0");Q0=makeQuery(id+"F0.imprint","IMPRINT",FACE,{"disambiguationData":[TD([[makeQuery(id+"F0.imprint","IMPRINT",EDGE,{"derivedFrom":subQ1}),1.0]])]});}
            var Q1;
            Q1=makeQuery(id+"F0.imprint","IMPRINT",FACE,{"disambiguationData":[TD([[makeQuery(id+"F0.imprint","IMPRINT",EDGE,{"derivedFrom":sQuery(id+"F0.wireOp",EDGE,"E1")}),1.0]])]});
            var Q2;
            Q2=makeQuery(id+"F0.imprint","IMPRINT",FACE,{"disambiguationData":[TD([[makeQuery(id+"F0.imprint","IMPRINT",EDGE,{"derivedFrom":sQuery(id+"F0.wireOp",EDGE,"89e0f370-7dde-42f9-8dba-64da66d548ce")}),1.0]])]});
            var Q3;
            {var subQ1=sQuery(id+"F0.wireOp",EDGE,"E129");var subQ12=sQuery(id+"F0.wireOp",EDGE,"E86");var subQ14=makeQuery(id+"F0.imprint","INTERSECT",VERTEX,{"derivedFrom":[subQ12,subQ1]});Q3=makeQuery(id+"F0.imprint","IMPRINT",FACE,{"disambiguationData":[TD([[makeQuery(id+"F0.imprint","IMPRINT",EDGE,{"disambiguationData":[TD([[subQ14,-1.0]])],"derivedFrom":subQ1}),1.0]])]});}
            var Q4;
            {var subQ0=sQuery(id+"F0.wireOp",EDGE,"E130");var subQ1=sQuery(id+"F0.wireOp",EDGE,"E129");var subQ6=makeQuery(id+"F0.imprint","INTERSECT",VERTEX,{"disambiguationData":[OD(0.0)],"derivedFrom":[subQ1,subQ0]});Q4=makeQuery(id+"F0.imprint","IMPRINT",FACE,{"disambiguationData":[TD([[makeQuery(id+"F0.imprint","IMPRINT",EDGE,{"disambiguationData":[TD([[subQ6,-1.0]])],"derivedFrom":subQ0}),-1.0]])]});}
            var Q5;
            {var subQ0=sQuery(id+"F0.wireOp",EDGE,"E132");var subQ6=sQuery(id+"F0.wireOp",EDGE,"E129");var subQ10=makeQuery(id+"F0.imprint","INTERSECT",VERTEX,{"disambiguationData":[OD(1.0)],"derivedFrom":[subQ6,subQ0]});Q5=makeQuery(id+"F0.imprint","IMPRINT",FACE,{"disambiguationData":[TD([[makeQuery(id+"F0.imprint","IMPRINT",EDGE,{"disambiguationData":[TD([[subQ10,-1.0]])],"derivedFrom":subQ6}),-1.0]])]});}
            var Q6;
            {var subQ0=sQuery(id+"F0.wireOp",EDGE,"E131");var subQ1=sQuery(id+"F0.wireOp",EDGE,"E129");var subQ2=makeQuery(id+"F0.imprint","INTERSECT",VERTEX,{"disambiguationData":[OD(0.0)],"derivedFrom":[subQ1,subQ0]});Q6=makeQuery(id+"F0.imprint","IMPRINT",FACE,{"disambiguationData":[TD([[makeQuery(id+"F0.imprint","IMPRINT",EDGE,{"disambiguationData":[TD([[subQ2,-1.0]])],"derivedFrom":subQ1}),-1.0]])]});}
            var Q7;
            Q7=makeQuery(id+"F0.imprint","IMPRINT",FACE,{"disambiguationData":[TD([[makeQuery(id+"F0.imprint","IMPRINT",EDGE,{"derivedFrom":sQuery(id+"F0.wireOp",EDGE,"E17")}),-1.0]])]});
            var Q8;
            Q8=makeQuery(id+"F0.imprint","IMPRINT",FACE,{"disambiguationData":[TD([[makeQuery(id+"F0.imprint","IMPRINT",EDGE,{"derivedFrom":sQuery(id+"F0.wireOp",EDGE,"E88")}),1.0]])]});
            var Q9;
            Q9=makeQuery(id+"F0.imprint","IMPRINT",FACE,{"disambiguationData":[TD([[makeQuery(id+"F0.imprint","IMPRINT",EDGE,{"derivedFrom":sQuery(id+"F0.wireOp",EDGE,"E102")}),-1.0]])]});
            var Q10;
            Q10=makeQuery(id+"F0.imprint","IMPRINT",FACE,{"disambiguationData":[TD([[makeQuery(id+"F0.imprint","IMPRINT",EDGE,{"derivedFrom":sQuery(id+"F0.wireOp",EDGE,"E117")}),1.0]])]});
            var Q11;
            Q11=makeQuery(id+"F0.imprint","IMPRINT",FACE,{"disambiguationData":[TD([[makeQuery(id+"F0.imprint","IMPRINT",EDGE,{"derivedFrom":sQuery(id+"F0.wireOp",EDGE,"E36")}),1.0]])]});
            var Q12;
            Q12=makeQuery(id+"F0.imprint","IMPRINT",FACE,{"disambiguationData":[TD([[makeQuery(id+"F0.imprint","IMPRINT",EDGE,{"derivedFrom":sQuery(id+"F0.wireOp",EDGE,"E32")}),-1.0]])]});
            var Q13;
            Q13=makeQuery(id+"F0.imprint","IMPRINT",FACE,{"disambiguationData":[TD([[makeQuery(id+"F0.imprint","IMPRINT",EDGE,{"derivedFrom":sQuery(id+"F0.wireOp",EDGE,"E18")}),-1.0]])]});
            var Q14;
            Q14=makeQuery(id+"F0.imprint","IMPRINT",FACE,{"disambiguationData":[TD([[makeQuery(id+"F0.imprint","IMPRINT",EDGE,{"derivedFrom":sQuery(id+"F0.wireOp",EDGE,"E44")}),-1.0]])]});
            var Q15;
            Q15=makeQuery(id+"F0.imprint","IMPRINT",FACE,{"disambiguationData":[TD([[makeQuery(id+"F0.imprint","IMPRINT",EDGE,{"derivedFrom":sQuery(id+"F0.wireOp",EDGE,"E48")}),-1.0]])]});
            var Q16;
            {var subQ5=sQuery(id+"F0.wireOp",EDGE,"E8");Q16=makeQuery(id+"F0.imprint","IMPRINT",FACE,{"disambiguationData":[TD([[makeQuery(id+"F0.imprint","IMPRINT",EDGE,{"derivedFrom":subQ5}),1.0]])]});}
            var Q17;
            Q17=makeQuery(id+"F0.imprint","IMPRINT",FACE,{"disambiguationData":[TD([[makeQuery(id+"F0.imprint","IMPRINT",EDGE,{"derivedFrom":sQuery(id+"F0.wireOp",EDGE,"E12")}),1.0]])]});
            var Q18;
            Q18=makeQuery(id+"F0.imprint","IMPRINT",FACE,{"disambiguationData":[TD([[makeQuery(id+"F0.imprint","IMPRINT",EDGE,{"derivedFrom":sQuery(id+"F0.wireOp",EDGE,"E70")}),-1.0]])]});
            var Q19;
            Q19=makeQuery(id+"F0.imprint","IMPRINT",FACE,{"disambiguationData":[TD([[makeQuery(id+"F0.imprint","IMPRINT",EDGE,{"derivedFrom":sQuery(id+"F0.wireOp",EDGE,"E225")}),1.0]])]});
            var Q20;
            Q20=makeQuery(id+"F0.imprint","IMPRINT",FACE,{"disambiguationData":[TD([[makeQuery(id+"F0.imprint","IMPRINT",EDGE,{"derivedFrom":sQuery(id+"F0.wireOp",EDGE,"E250")}),1.0]])]});
            var Q21;
            Q21=makeQuery(id+"F0.imprint","IMPRINT",FACE,{"disambiguationData":[TD([[makeQuery(id+"F0.imprint","IMPRINT",EDGE,{"derivedFrom":sQuery(id+"F0.wireOp",EDGE,"E106")}),1.0]])]});
            extrude(context, id + "F1", {"entities" : qUnion([Q0, Q1, Q2, Q3, Q4, Q5, Q6, Q7, Q8, Q9, Q10, Q11, Q12, Q13, Q14, Q15, Q16, Q17, Q18, Q19, Q20, Q21]), "depth" : 12.7 * mm, "hasSecondDirection" : true, "secondDirectionOppositeDirection" : true, "secondDirectionDepth" : 12.7 * mm});
        }
    });
